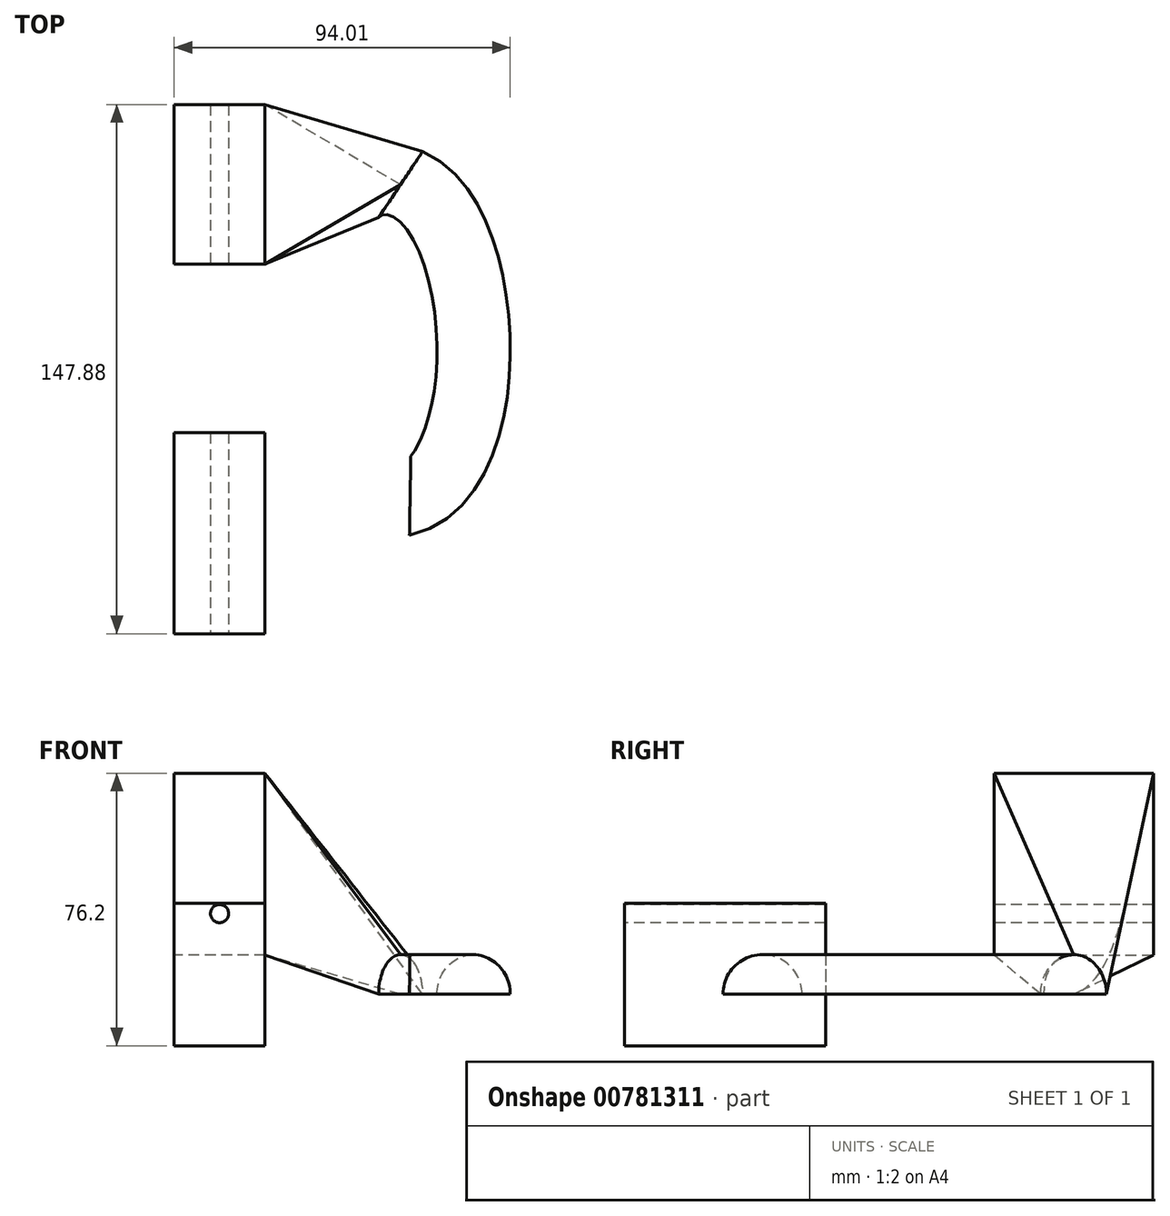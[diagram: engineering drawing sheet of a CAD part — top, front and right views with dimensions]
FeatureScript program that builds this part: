
annotation { "Feature Type Name" : "Feature", "Feature Type Description" : "" }
export const myFeature = defineFeature(function(context is Context, id is Id, definition is map)
    precondition{}
    {
        {
            var Q0;
            Q0=qCreatedBy(makeId("Right.planeOp"),FACE);
            var sketch = newSketch(context, id + "F0", { "sketchPlane" : qUnion([Q0])});
            skLineSegment(sketch, "E0.bottom", {"start": v(-56.16, 39.8) * mm, "end": v(0, 39.8) * mm});
            skLineSegment(sketch, "E0.top", {"start": v(-56.16, 0) * mm, "end": v(0, 0) * mm});
            skLineSegment(sketch, "E0.left", {"start": v(-56.16, 39.8) * mm, "end": v(-56.16, 0) * mm});
            skLineSegment(sketch, "E0.right", {"start": v(0, 39.8) * mm, "end": v(0, 0) * mm});
            skLineSegment(sketch, "E1.bottom", {"start": v(47.13, 76.2) * mm, "end": v(91.72, 76.2) * mm});
            skLineSegment(sketch, "E1.top", {"start": v(47.13, 25.4) * mm, "end": v(91.72, 25.4) * mm});
            skLineSegment(sketch, "E1.left", {"start": v(47.13, 76.2) * mm, "end": v(47.13, 25.4) * mm});
            skLineSegment(sketch, "E1.right", {"start": v(91.72, 76.2) * mm, "end": v(91.72, 25.4) * mm});
            skSolve(sketch);
        }
        {
            var Q0;
            Q0=makeQuery(id+"F0.imprint","IMPRINT",FACE,{"disambiguationData":[TD([[makeQuery(id+"F0.imprint","IMPRINT",EDGE,{"derivedFrom":sQuery(id+"F0.wireOp",EDGE,"E0.bottom")}),-1.0]])]});
            var Q1;
            Q1=makeQuery(id+"F0.imprint","IMPRINT",FACE,{"disambiguationData":[TD([[makeQuery(id+"F0.imprint","IMPRINT",EDGE,{"derivedFrom":sQuery(id+"F0.wireOp",EDGE,"E1.bottom")}),-1.0]])]});
            extrude(context, id + "F1", {"entities" : qUnion([Q0, Q1]), "endBound" : BoundingType.SYMMETRIC, "depth" : 25.4 * mm, "offsetDistance" : 25.4 * mm});
        }
        {
            var Q0;
            Q0=makeQuery(id+"F1.opExtrude","SWEPT_FACE",FACE,{"disambiguationData":[OSD([sQuery(id+"F0.wireOp",EDGE,"E0.left")])]});
            cPlane(context, id + "F2", {"entities" : qUnion([Q0]), "cplaneType" : CPlaneType.OFFSET, "offset" : 0 * mm, "width" : 152.4 * mm, "height" : 152.4 * mm});
        }
        {
            var Q0;
            Q0=qCreatedBy(id+"F2.planeOp",FACE);
            var sketch = newSketch(context, id + "F3", { "sketchPlane" : qUnion([Q0])});
            skCircle(sketch, "E2", {"center": v(0, 36.96) * mm, "radius": 2.42 * mm});
            skSolve(sketch);
        }
        {
            var Q0;
            Q0=makeQuery(id+"F1.opExtrude","SWEPT_FACE",FACE,{"disambiguationData":[OSD([sQuery(id+"F0.wireOp",EDGE,"E0.bottom")])]});
            cPlane(context, id + "F4", {"entities" : qUnion([Q0]), "cplaneType" : CPlaneType.OFFSET, "offset" : 25.4 * mm, "oppositeDirection" : true, "width" : 152.4 * mm, "height" : 152.4 * mm});
        }
        {
            var Q0;
            Q0=qCreatedBy(id+"F4.planeOp",FACE);
            var sketch = newSketch(context, id + "F5", { "sketchPlane" : qUnion([Q0])});
            skFitSpline(sketch, "E3", {"points": [v(53.32, -17.63) * mm, v(50.62, 69.4) * mm], "startDerivative": vector(79.76, 30.6) * mm, "endDerivative": vector(-71.32, 14.78) * mm});
            skSolve(sketch);
        }
        {
            var Q0;
            Q0=makeQuery(id+"F1.opExtrude","CAP_FACE",FACE,{"disambiguationData":[OSD([sQuery(id+"F0.wireOp",EDGE,"E0.bottom"),sQuery(id+"F0.wireOp",EDGE,"E0.top"),sQuery(id+"F0.wireOp",EDGE,"E0.left"),sQuery(id+"F0.wireOp",EDGE,"E0.right")])],"isStart":false});
            cPlane(context, id + "F6", {"entities" : qUnion([Q0]), "cplaneType" : CPlaneType.OFFSET, "offset" : 40.9 * mm, "width" : 152.4 * mm, "height" : 152.4 * mm});
        }
        {
            var Q0;
            Q0=qCreatedBy(id+"F6.planeOp",FACE);
            var sketch = newSketch(context, id + "F7", { "sketchPlane" : qUnion([Q0])});
            skArc(sketch, "E4", {"start": v(-6.46, 14.4) * mm, "mid": v(-17.52, 25.45) * mm, "end": v(-28.57, 14.4) * mm});
            skLineSegment(sketch, "E5", {"start": v(-28.57, 14.4) * mm, "end": v(-6.46, 14.4) * mm});
            skSolve(sketch);
        }
        {
            var Q0;
            Q0=makeQuery(id+"F7.imprint","IMPRINT",FACE,{"disambiguationData":[TD([[makeQuery(id+"F7.imprint","IMPRINT",EDGE,{"derivedFrom":sQuery(id+"F7.wireOp",EDGE,"E4")}),1.0]])]});
            var Q1;
            Q1=sQuery(id+"F5.wireOp",EDGE,"E3");
            sweep(context, id + "F8", {"profiles" : qUnion([Q0]), "path" : qUnion([Q1])});
        }
        {
            var Q0;
            Q0=makeQuery(id+"F8.opSweep","CAP_FACE",FACE,{"disambiguationData":[OSD([sQuery(id+"F5.wireOp",VERTEX,"E3.end"),sQuery(id+"F7.wireOp",EDGE,"E4"),sQuery(id+"F7.wireOp",EDGE,"E5")])],"isStart":false});
            var Q1;
            Q1=makeQuery(id+"F1.opExtrude","CAP_FACE",FACE,{"disambiguationData":[OSD([sQuery(id+"F0.wireOp",EDGE,"E1.bottom"),sQuery(id+"F0.wireOp",EDGE,"E1.top"),sQuery(id+"F0.wireOp",EDGE,"E1.left"),sQuery(id+"F0.wireOp",EDGE,"E1.right")])],"isStart":false});
            var Q2;
            Q2=makeQuery(id+"F8.opSweep","CAP_FACE",FACE,{"disambiguationData":[OSD([sQuery(id+"F5.wireOp",VERTEX,"E3.end"),sQuery(id+"F7.wireOp",EDGE,"E4"),sQuery(id+"F7.wireOp",EDGE,"E5")])],"isStart":false});
            var Q3;
            Q3=makeQuery(id+"F1.opExtrude","CAP_FACE",FACE,{"disambiguationData":[OSD([sQuery(id+"F0.wireOp",EDGE,"E1.bottom"),sQuery(id+"F0.wireOp",EDGE,"E1.top"),sQuery(id+"F0.wireOp",EDGE,"E1.left"),sQuery(id+"F0.wireOp",EDGE,"E1.right")])],"isStart":false});
            loft(context, id + "F9", {"surfaceOperationType" : NewSurfaceOperationType.ADD, "sheetProfilesArray" : [{ "sheetProfileEntities" : qUnion([Q0]) }, { "sheetProfileEntities" : qUnion([Q1]) }], "wireProfilesArray" : [{ "wireProfileEntities" : qUnion([Q2]) }, { "wireProfileEntities" : qUnion([Q3]) }]});
        }
        {
            var Q0;
            Q0=sQuery(id+"F3.wireOp",VERTEX,"E2.center");
            var Q1;
            Q1=makeQuery(id+"F1.opExtrude","SWEPT_BODY",BODY,{"disambiguationData":[OSD([sQuery(id+"F0.wireOp",EDGE,"E0.bottom"),sQuery(id+"F0.wireOp",EDGE,"E0.top"),sQuery(id+"F0.wireOp",EDGE,"E0.left"),sQuery(id+"F0.wireOp",EDGE,"E0.right")])]});
            var Q2;
            Q2=makeQuery(id+"F1.opExtrude","SWEPT_BODY",BODY,{"disambiguationData":[OSD([sQuery(id+"F0.wireOp",EDGE,"E1.bottom"),sQuery(id+"F0.wireOp",EDGE,"E1.top"),sQuery(id+"F0.wireOp",EDGE,"E1.left"),sQuery(id+"F0.wireOp",EDGE,"E1.right")])]});
            hole(context, id + "F10", {"style" : HoleStyle.SIMPLE, "endStyle" : HoleEndStyle.THROUGH, "holeDiameter" : 5.08 * mm, "majorDiameter" : 6.35 * mm, "isTappedThrough" : true, "tappedDepth" : 12.7 * mm, "tapClearance" : 3, "locations" : qUnion([Q0]), "scope" : qUnion([Q1, Q2])});
        }
    });
